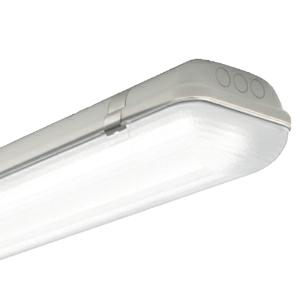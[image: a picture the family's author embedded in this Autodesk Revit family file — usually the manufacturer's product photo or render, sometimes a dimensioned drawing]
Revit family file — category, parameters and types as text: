
# Revit family: 3f_filippi_-_3f_linda_soft_3f_filippi_-_58751_-_3f_linda_led_soft_2x22w_l1570
name_source: partatom
category: Lighting Fixtures
units: mm (PartAtom-declared; Revit-internal decimal feet)

## family parameters
Cut with Voids When Loaded = No
Host = Face
Light Source = No
Part Type = Normal
Room Calculation Point = No
Round Connector Dimension = Use Diameter
Shared = No

## types (1)
- 3F Filippi - 3F Linda Soft (1 x LED, 6835 lm, 49 W, 4000 K)
    Apparent Load = 49 VA
    Approval mark = CE
    CIE Flux Codes = 42 72 91 93 100
    Color Rendering = 80
    Color Temperature = 4000 K
    Control Gear = Electronic ballast
    Default Elevation = 1800 mm
    Description = ILLUMINOTECHNICAL
Luminous efficiency 100% (DLOR 93%, ULOR 7%).
Initial luminous flux of the luminaire 6835 lm.
Direct symmetric distribution.
Installation Interdistance Transv.D = 1.35 x hu - Long.D = 1.24 x hu.
Tabular UGR (CIE 117 - 4H-8H; S=0.25H; 70/50/20): RUG 23.7 - 21.8.
Beam angle: 131° - 111°.
Luminous efficacy 139 lm/W.
Lifetime (L93/B10): 30000 h. (tq+25°C)
Lifetime (L90/B10): 50000 h. (tq+25°C)
Lifetime (L85/B10): 80000 h. (tq+25°C)
Lifetime (L80/B10): 100000 h. (tq+25°C)
Lifetime (L85/B10): 50000 h. (tq+40°C)
Sudden decreased luminous flux after 50000 hours: 0% (C0).
Photobiological safety in compliance with IEC/TR 62778: RG0 risk exempt, (IEC 62471).
In compliance with IEC/EN 62722-2-1 - IEC/EN 62717 standards.

SOURCE
2 linear LED modules 22W/840.
Energy efficiency class (UE 2019/2020 - UE 2019/2015): D.
CIE 13.3 Colour rendering index: CRI >80 (R9 <50%).
IES TM-30 Fidelity Index: Rf = 84 Rg = 95.
CCT nominal colour temperature 4000 K.
Colour initial tolerance (MacAdam): SDCM 3.

MECHANICAL
Self-extinguishing V2 polycarbonate housing, injection moulded, RAL 7035 grey.
Ecologic anti-aging injected sealing gasket.
Soft opal diffuser in self-extinguishing V2 polycarbonate, photo-engraved interior, UV stabilised, injection moulded.
Gear-holder reflector in hot-dip galvanised steel, painted with white polyester base.
Snug fit safety snap-lock clips for diffuser mounting in stainless steel, screwdriver opening.
Fixing brackets in stainless steel.
Possibility for technicians to access the interior of the luminaire.
Luminaire with limited surface temperature. - D - (EN 60598-2-24)
Dimensions: 1570x160 mm, height 100 mm. Weight 3.26 kg.
IP66 protection degree.
Mechanical strength to impacts IK10 (20 joule).
Glow-wire test resistance 850°C.

ELECTRICAL
Halogen Free electronic wiring 230V-50/60Hz, power factor 0.97, THD <25%, constant output current, SELV, class I, 1 driver.
Power of the luminaire 49 W.
ENEC - CE.
SAFE FLICKER: PstLM=<1 and SVM=<0.4 (IEC TR 61547-1 and IEC TR 63158), to ensure a more comfortable and safe light.
Luminaire compliant with EN 60598-2-22 for power supply from a centralised emergency system CPSS (Central Power Supply System), not incorporated in the luminaire - high risk areas excluded. The default power and flux are 100% in AC and 100% in DC.
Ambient temperature from -20°C to +40°C.
Temperature class T6 max 85°C.
Relative humidity UR: <85%.

INSTALLATION
Ceiling / Suspended / Wall.
All accessories dedicated to this product are available on the Catalog and on our website www.3F-Filippi.com.

APPLICATIONS
Suitable product for food production plants (HACCP), IFS (Food Version 6), BRC (GSFS Food Version 7).
Dry, dusty indoor environments, subject to occasional water splashes.
Luminaires designed for diffuse direct/indirect lighting suitable to provide optimum visual comfort.
Transit areas, stairwells.
Virtually shatterproof polycarbonate compatibly with the fumes / atmospheres that compromise the elasticity of plastic materials.
Suitable for illumination of public car parks and parking grounds referred to DIN 67528:2018-04.

WARNING
Fixture not suitable for cold stores with an ambient temperature <0°C and/or relative humidity >85%.
Luminaire designed for disposal/recycling at end-of-life.
Replaceable (LED only) light source by a professional. Replaceable control gear by a professional.
    Height = 100 mm  [stored 0.328084 ft]
    Lamp = 1 x LED
    Lamp Light Flux = 6835 lm
    Lamp Power = 49 W
    Lamp count = 1
    Length = 1570 mm
    Lifetime = 50000 h
    Luminous efficacy = 139 lm/W
    Manufacturer = 3F Filippi
    ModVariant = No
    Model = 3F Filippi - 58751 - 3F Linda LED Soft 2x22W L1570
    Mounting Place = Ceiling
    Mounting Type = Pendant
    Number of Poles = 1
    OnlyDefault = Yes
    Power Factor = 1
    Product Name = 3F Filippi - 3F Linda Soft
    Product group = pendant luminaire
    ProductGroupID = 9
    Protection Class = Protection class I
    Protection Degree = IP 66
    RLX_Detail_Level = 1
    RLX_Emergency_Light_Flux = 0 lm
    RLX_Emergency_Type = 0
    RLX_Emergency_Type_DB = No
    RlxData = <blob elided: 69405 chars, md5=23c583fa>
    Socket = socket
    Standby Power = 0 W
    System Light Flux = 6835 lm
    System Power = 49 W
    Type Comments = Product without accessories
    Type Image = 3ffilippi_3f_linda_led_soft_2x.jpg
    URL = http://relux.com
    VarID = ---
    Voltage = 0 V
    Weight = 0.00 kg
    Width = 160 mm

note: [stored X ft] marks values corroborated as IEEE doubles in the binary element streams (Revit-internal decimal feet)

## geometry (parser evidence)
native form markers: Blend x4, Sweep x14
no freeform markers — native parametric forms only
